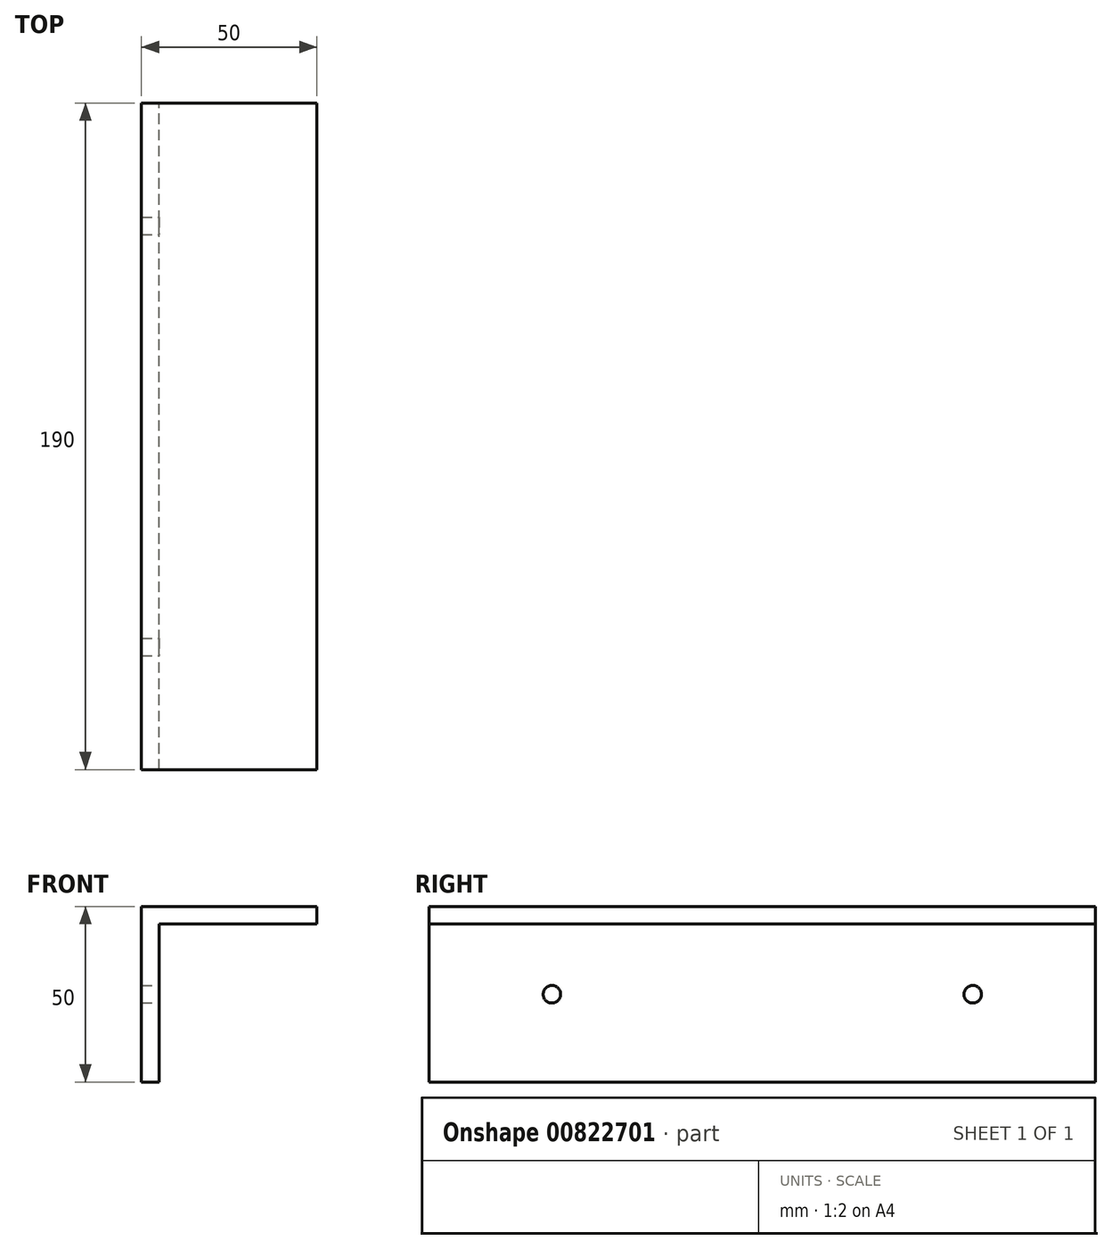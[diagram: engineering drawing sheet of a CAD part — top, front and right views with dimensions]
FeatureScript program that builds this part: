
annotation { "Feature Type Name" : "Feature", "Feature Type Description" : "" }
export const myFeature = defineFeature(function(context is Context, id is Id, definition is map)
    precondition{}
    {
        {
            var Q0;
            Q0=qCreatedBy(makeId("Front.planeOp"),FACE);
            var sketch = newSketch(context, id + "F0", { "sketchPlane" : qUnion([Q0])});
            skLineSegment(sketch, "E0", {"start": v(0, 0) * mm, "end": v(0, 50) * mm});
            skLineSegment(sketch, "E1", {"start": v(0, 50) * mm, "end": v(50, 50) * mm});
            skLineSegment(sketch, "E2", {"start": v(50, 50) * mm, "end": v(50, 45) * mm});
            skLineSegment(sketch, "E3", {"start": v(50, 45) * mm, "end": v(5, 45) * mm});
            skLineSegment(sketch, "E4", {"start": v(5, 45) * mm, "end": v(5, 0) * mm});
            skLineSegment(sketch, "E5", {"start": v(5, 0) * mm, "end": v(0, 0) * mm});
            skSolve(sketch);
        }
        {
            var Q0;
            Q0 = qSketchRegion(id + "F0", true);
            extrude(context, id + "F1", {"entities" : qUnion([Q0]), "depth" : 190 * mm, "offsetDistance" : 25 * mm});
        }
        {
            var Q0;
            Q0=makeQuery(id+"F1.opExtrude","SWEPT_FACE",FACE,{"disambiguationData":[OSD([sQuery(id+"F0.wireOp",EDGE,"E4")])]});
            var sketch = newSketch(context, id + "F2", { "sketchPlane" : qUnion([Q0])});
            skPoint(sketch, "E6", {"position": v(-155, 25) * mm});
            skPoint(sketch, "E7", {"position": v(-35, 25) * mm});
            skSolve(sketch);
        }
        {
            var Q0;
            Q0=sQuery(id+"F2.wireOp",VERTEX,"E6");
            var Q1;
            Q1=sQuery(id+"F2.wireOp",VERTEX,"E7");
            var Q2;
            Q2=makeQuery(id+"F1.opExtrude","SWEPT_BODY",BODY,{"disambiguationData":[OSD([sQuery(id+"F0.wireOp",EDGE,"E0"),sQuery(id+"F0.wireOp",EDGE,"E1"),sQuery(id+"F0.wireOp",EDGE,"E2"),sQuery(id+"F0.wireOp",EDGE,"E3"),sQuery(id+"F0.wireOp",EDGE,"E4"),sQuery(id+"F0.wireOp",EDGE,"E5")])]});
            hole(context, id + "F3", {"style" : HoleStyle.SIMPLE, "endStyle" : HoleEndStyle.THROUGH, "holeDiameter" : 5 * mm, "majorDiameter" : 5 * mm, "isTappedThrough" : true, "tappedDepth" : 12 * mm, "tapClearance" : 3, "locations" : qUnion([Q0, Q1]), "scope" : qUnion([Q2])});
        }
    });
